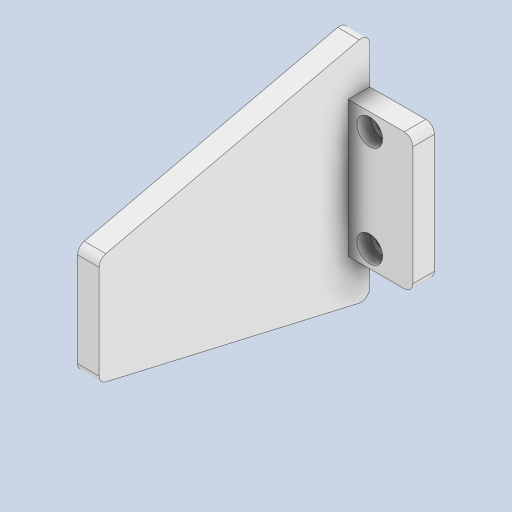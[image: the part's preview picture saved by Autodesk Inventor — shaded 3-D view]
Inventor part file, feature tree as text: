
AUTODESK INVENTOR PART (.ipt)
format: ipt  version: 2023 (Build 270158000, 158)  size: 158,720 bytes
history: native  units: in
note: dims shown in document units (in); Inventor stores cm internally (conversion verified against a paired STEP export)
features: sketch x3, extrude x2, other x1, hole x1, fillet x1
ambient origin geometry x8: Origin, YZ Plane, XZ Plane, XY Plane, X Axis, Y Axis, Z Axis, Center Point
bodies: Body1 (feature_tree)
feature tree (8):
  other  "ソリッド1"
  extrude  "押し出し1"  Depth=0.5291in
  extrude  "押し出し2"  Depth=0.5291in
  hole  "穴1"  [1 undecoded]
  fillet  "フィレット1"  Radius=2.126in
  sketch  "スケッチ1"
  sketch  "スケッチ2"
  sketch  "スケッチ3"
note: 1 required parameter value undecoded (feature->parameter linkage not recoverable at this tier; creation-order binding heuristic only, values carry confidence <= 0.55)
